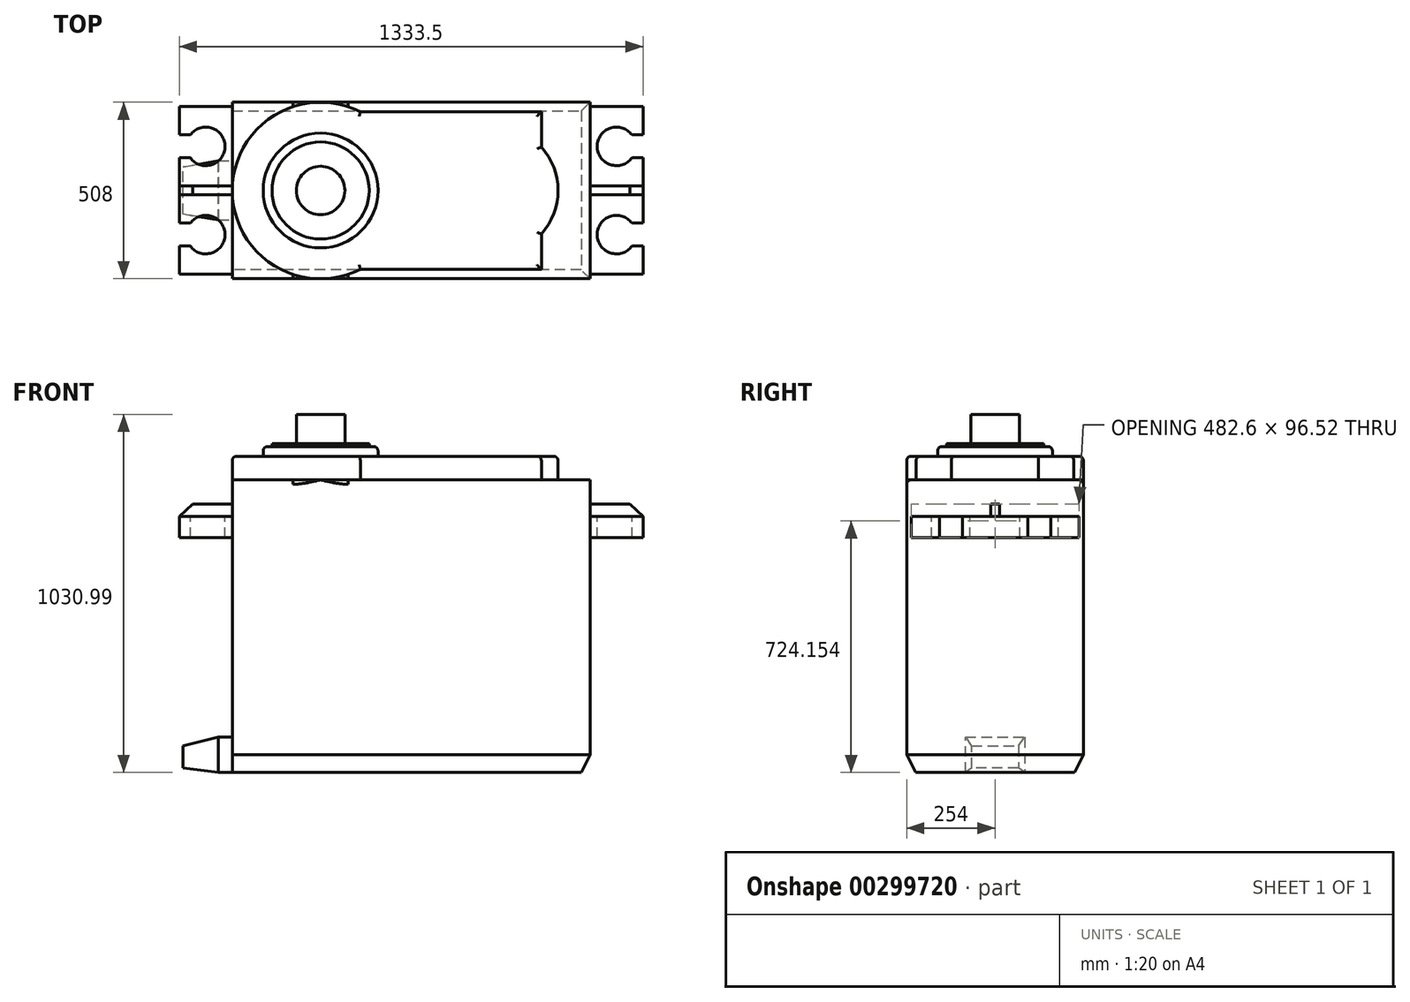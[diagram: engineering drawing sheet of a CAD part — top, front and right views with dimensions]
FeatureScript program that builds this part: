
annotation { "Feature Type Name" : "Feature", "Feature Type Description" : "" }
export const myFeature = defineFeature(function(context is Context, id is Id, definition is map)
    precondition{}
    {
        {
            var Q0;
            Q0=qCreatedBy(makeId("Front.planeOp"),FACE);
            var sketch = newSketch(context, id + "F0", { "sketchPlane" : qUnion([Q0])});
            skLineSegment(sketch, "E0", {"start": v(0, 0) * mm, "end": v(514.35, 0) * mm});
            skLineSegment(sketch, "E1.MirrorCS", {"start": v(0, 0) * mm, "end": v(-514.35, 0) * mm});
            skLineSegment(sketch, "E2", {"start": v(514.35, 0) * mm, "end": v(514.35, 842.26) * mm});
            skLineSegment(sketch, "E3", {"start": v(514.35, 842.26) * mm, "end": v(-514.35, 842.26) * mm});
            skLineSegment(sketch, "E4", {"start": v(-514.35, 842.26) * mm, "end": v(-514.35, 0) * mm});
            skSolve(sketch);
        }
        {
            var Q0;
            Q0 = qSketchRegion(id + "F0", true);
            extrude(context, id + "F1", {"entities" : qUnion([Q0]), "endBound" : BoundingType.SYMMETRIC, "depth" : 508 * mm});
        }
        {
            var Q0;
            Q0=makeQuery(id+"F1.opExtrude","CAP_EDGE",EDGE,{"disambiguationData":[OSD([sQuery(id+"F0.wireOp",EDGE,"E0"),sQuery(id+"F0.wireOp",EDGE,"E1.MirrorCS")])],"isStart":false});
            var Q1;
            Q1=makeQuery(id+"F1.opExtrude","SWEPT_EDGE",EDGE,{"disambiguationData":[OSD([sQuery(id+"F0.wireOp",EDGE,"E0"),sQuery(id+"F0.wireOp",EDGE,"E2")])]});
            var Q2;
            Q2=makeQuery(id+"F1.opExtrude","CAP_EDGE",EDGE,{"disambiguationData":[OSD([sQuery(id+"F0.wireOp",EDGE,"E0"),sQuery(id+"F0.wireOp",EDGE,"E1.MirrorCS")])],"isStart":true});
            chamfer(context, id + "F2", {"entities" : qUnion([Q0, Q1, Q2]), "chamferType" : ChamferType.OFFSET_ANGLE, "width" : 25.4 * mm, "oppositeDirection" : false, "angle" : 63.4 * degree, "tangentPropagation" : true});
        }
        {
            var Q0;
            Q0=makeQuery(id+"F1.opExtrude","SWEPT_FACE",FACE,{"disambiguationData":[OSD([sQuery(id+"F0.wireOp",EDGE,"E4")])]});
            var sketch = newSketch(context, id + "F3", { "sketchPlane" : qUnion([Q0])});
            skLineSegment(sketch, "E5", {"start": v(-85.09, 0) * mm, "end": v(85.1, 0) * mm});
            skLineSegment(sketch, "E6", {"start": v(85.1, 0) * mm, "end": v(85.1, 101.6) * mm});
            skLineSegment(sketch, "E7", {"start": v(85.1, 101.6) * mm, "end": v(-85.09, 101.6) * mm});
            skLineSegment(sketch, "E8", {"start": v(-85.09, 101.6) * mm, "end": v(-85.09, 0) * mm});
            skSolve(sketch);
        }
        {
            var Q0;
            Q0 = qSketchRegion(id + "F3", true);
            extrude(context, id + "F4", {"entities" : qUnion([Q0]), "operationType" : NewBodyOperationType.ADD, "depth" : 142.24 * mm});
        }
        {
            var Q0;
            Q0=makeQuery(id+"F4.opExtrude","CAP_EDGE",EDGE,{"disambiguationData":[OSD([sQuery(id+"F3.wireOp",EDGE,"E5")])],"isStart":false});
            chamfer(context, id + "F5", {"entities" : qUnion([Q0]), "chamferType" : ChamferType.TWO_OFFSETS, "width1" : 101.6 * mm, "oppositeDirection" : false, "width2" : 12.7 * mm, "tangentPropagation" : true});
        }
        {
            var Q0;
            Q0=makeQuery(id+"F4.opExtrude","CAP_EDGE",EDGE,{"disambiguationData":[OSD([sQuery(id+"F3.wireOp",EDGE,"E6")])],"isStart":false});
            var Q1;
            Q1=makeQuery(id+"F4.opExtrude","CAP_EDGE",EDGE,{"disambiguationData":[OSD([sQuery(id+"F3.wireOp",EDGE,"E8")])],"isStart":false});
            chamfer(context, id + "F6", {"entities" : qUnion([Q0, Q1]), "chamferType" : ChamferType.TWO_OFFSETS, "width1" : 101.6 * mm, "oppositeDirection" : true, "width2" : 17.78 * mm, "tangentPropagation" : true});
        }
        {
            var Q0;
            Q0=makeQuery(id+"F4.opExtrude","CAP_EDGE",EDGE,{"disambiguationData":[OSD([sQuery(id+"F3.wireOp",EDGE,"E7")])],"isStart":false});
            chamfer(context, id + "F7", {"entities" : qUnion([Q0]), "chamferType" : ChamferType.TWO_OFFSETS, "width1" : 101.6 * mm, "oppositeDirection" : true, "width2" : 25.4 * mm, "tangentPropagation" : true});
        }
        {
            var Q0;
            Q0=makeQuery(id+"F1.opExtrude","SWEPT_FACE",FACE,{"disambiguationData":[OSD([sQuery(id+"F0.wireOp",EDGE,"E3")])]});
            var sketch = newSketch(context, id + "F8", { "sketchPlane" : qUnion([Q0])});
            skLineSegment(sketch, "E9", {"start": v(514.35, 0) * mm, "end": v(514.35, -241.3) * mm});
            skLineSegment(sketch, "E10", {"start": v(514.35, -241.3) * mm, "end": v(666.75, -241.3) * mm});
            skLineSegment(sketch, "E11", {"start": v(666.75, -241.3) * mm, "end": v(666.75, -160.02) * mm});
            skArc(sketch, "E12", {"start": v(635, -160.02) * mm, "mid": v(535.18, -127) * mm, "end": v(635, -93.98) * mm});
            skLineSegment(sketch, "E13", {"start": v(635, -160.02) * mm, "end": v(666.75, -160.02) * mm});
            skLineSegment(sketch, "E14", {"start": v(666.75, -93.98) * mm, "end": v(666.75, 0) * mm});
            skLineSegment(sketch, "E15", {"start": v(666.75, -93.98) * mm, "end": v(635, -93.98) * mm});
            skLineSegment(sketch, "E16", {"start": v(514.35, 0) * mm, "end": v(563.65, 0) * mm});
            skLineSegment(sketch, "E17.MirrorCS", {"start": v(514.35, 0) * mm, "end": v(514.35, 241.3) * mm});
            skLineSegment(sketch, "E18.MirrorCS", {"start": v(514.35, 241.3) * mm, "end": v(666.75, 241.3) * mm});
            skLineSegment(sketch, "E19.MirrorCS", {"start": v(666.75, 241.3) * mm, "end": v(666.75, 160.02) * mm});
            skArc(sketch, "E20.MirrorCS", {"start": v(635, 160.02) * mm, "mid": v(535.18, 127) * mm, "end": v(635, 93.98) * mm});
            skLineSegment(sketch, "E21.MirrorCS", {"start": v(666.75, 93.98) * mm, "end": v(666.75, 0) * mm});
            skLineSegment(sketch, "E22.MirrorCS", {"start": v(666.75, 93.98) * mm, "end": v(635, 93.98) * mm});
            skLineSegment(sketch, "E23.MirrorCS", {"start": v(635, 160.02) * mm, "end": v(666.75, 160.02) * mm});
            skLineSegment(sketch, "E24", {"start": v(0, 0) * mm, "end": v(0, -87.43) * mm});
            skLineSegment(sketch, "E25.MirrorCS", {"start": v(-514.35, 0) * mm, "end": v(-514.35, 241.3) * mm});
            skLineSegment(sketch, "E26.MirrorCS", {"start": v(-514.35, 0) * mm, "end": v(-514.35, -241.3) * mm});
            skLineSegment(sketch, "E27.MirrorCS", {"start": v(-666.75, -93.98) * mm, "end": v(-635, -93.98) * mm});
            skLineSegment(sketch, "E28.MirrorCS", {"start": v(-635, -160.02) * mm, "end": v(-666.75, -160.02) * mm});
            skLineSegment(sketch, "E29.MirrorCS", {"start": v(-635, 160.02) * mm, "end": v(-666.75, 160.02) * mm});
            skLineSegment(sketch, "E30.MirrorCS", {"start": v(-666.75, 93.98) * mm, "end": v(-635, 93.98) * mm});
            skLineSegment(sketch, "E31.MirrorCS", {"start": v(-514.35, 0) * mm, "end": v(-563.65, 0) * mm});
            skLineSegment(sketch, "E32.MirrorCS", {"start": v(-514.35, 241.3) * mm, "end": v(-666.75, 241.3) * mm});
            skLineSegment(sketch, "E33.MirrorCS", {"start": v(-666.75, 241.3) * mm, "end": v(-666.75, 160.02) * mm});
            skArc(sketch, "E34.MirrorCS", {"start": v(-635, 160.02) * mm, "mid": v(-535.18, 127) * mm, "end": v(-635, 93.98) * mm});
            skLineSegment(sketch, "E35.MirrorCS", {"start": v(-666.75, -93.98) * mm, "end": v(-666.75, 0) * mm});
            skLineSegment(sketch, "E36.MirrorCS", {"start": v(-666.75, 93.98) * mm, "end": v(-666.75, 0) * mm});
            skArc(sketch, "E37.MirrorCS", {"start": v(-635, -160.02) * mm, "mid": v(-535.18, -127) * mm, "end": v(-635, -93.98) * mm});
            skLineSegment(sketch, "E38.MirrorCS", {"start": v(-666.75, -241.3) * mm, "end": v(-666.75, -160.02) * mm});
            skLineSegment(sketch, "E39.MirrorCS", {"start": v(-514.35, -241.3) * mm, "end": v(-666.75, -241.3) * mm});
            skSolve(sketch);
        }
        {
            var Q0;
            Q0 = qSketchRegion(id + "F8", true);
            extrude(context, id + "F9", {"entities" : qUnion([Q0]), "operationType" : NewBodyOperationType.ADD, "oppositeDirection" : true, "depth" : 166.37 * mm});
        }
        {
            var Q0;
            Q0=makeQuery(id+"F8.imprint","IMPRINT",FACE,{"disambiguationData":[TD([[makeQuery(id+"F8.imprint","IMPRINT",EDGE,{"derivedFrom":sQuery(id+"F8.wireOp",EDGE,"E27.MirrorCS")}),1.0]])]});
            var Q1;
            Q1=makeQuery(id+"F8.imprint","IMPRINT",FACE,{"disambiguationData":[TD([[makeQuery(id+"F8.imprint","IMPRINT",EDGE,{"derivedFrom":sQuery(id+"F8.wireOp",EDGE,"E9")}),-1.0]])]});
            extrude(context, id + "F10", {"entities" : qUnion([Q0, Q1]), "operationType" : NewBodyOperationType.REMOVE, "oppositeDirection" : true, "depth" : 105.4 * mm});
        }
        {
            var Q0;
            Q0=makeQuery(id+"F10.boolean.opBoolean","COPY",FACE,{"derivedFrom":makeQuery(id+"F10.opExtrude","CAP_FACE",FACE,{"disambiguationData":[OSD([sQuery(id+"F8.wireOp",EDGE,"E9"),sQuery(id+"F8.wireOp",EDGE,"E10"),sQuery(id+"F8.wireOp",EDGE,"E11"),sQuery(id+"F8.wireOp",EDGE,"E12"),sQuery(id+"F8.wireOp",EDGE,"E13"),sQuery(id+"F8.wireOp",EDGE,"E14"),sQuery(id+"F8.wireOp",EDGE,"E15"),sQuery(id+"F8.wireOp",EDGE,"E17.MirrorCS"),sQuery(id+"F8.wireOp",EDGE,"E18.MirrorCS"),sQuery(id+"F8.wireOp",EDGE,"E19.MirrorCS"),sQuery(id+"F8.wireOp",EDGE,"E20.MirrorCS"),sQuery(id+"F8.wireOp",EDGE,"E21.MirrorCS"),sQuery(id+"F8.wireOp",EDGE,"E22.MirrorCS"),sQuery(id+"F8.wireOp",EDGE,"E23.MirrorCS")])],"isStart":false})});
            var sketch = newSketch(context, id + "F11", { "sketchPlane" : qUnion([Q0])});
            skLineSegment(sketch, "E40", {"start": v(514.35, -12.7) * mm, "end": v(666.75, -12.7) * mm});
            skLineSegment(sketch, "E41", {"start": v(666.75, -12.7) * mm, "end": v(666.75, 12.7) * mm});
            skLineSegment(sketch, "E42", {"start": v(666.75, 12.7) * mm, "end": v(514.35, 12.7) * mm});
            skLineSegment(sketch, "E43", {"start": v(514.35, 12.7) * mm, "end": v(514.35, -12.7) * mm});
            skLineSegment(sketch, "E44", {"start": v(0, 0) * mm, "end": v(0, 98.08) * mm});
            skLineSegment(sketch, "E45.MirrorCS", {"start": v(-666.75, -12.7) * mm, "end": v(-666.75, 12.7) * mm});
            skLineSegment(sketch, "E46.MirrorCS", {"start": v(-514.35, 12.7) * mm, "end": v(-514.35, -12.7) * mm});
            skLineSegment(sketch, "E47.MirrorCS", {"start": v(-514.35, -12.7) * mm, "end": v(-666.75, -12.7) * mm});
            skLineSegment(sketch, "E48.MirrorCS", {"start": v(-666.75, 12.7) * mm, "end": v(-514.35, 12.7) * mm});
            skSolve(sketch);
        }
        {
            var Q0;
            Q0 = qSketchRegion(id + "F11", true);
            extrude(context, id + "F12", {"entities" : qUnion([Q0]), "operationType" : NewBodyOperationType.ADD, "depth" : 35.56 * mm});
        }
        {
            var Q0;
            Q0=makeQuery(id+"F12.opExtrude","CAP_EDGE",EDGE,{"disambiguationData":[OSD([sQuery(id+"F11.wireOp",EDGE,"E41")])],"isStart":false});
            chamfer(context, id + "F13", {"entities" : qUnion([Q0]), "chamferType" : ChamferType.TWO_OFFSETS, "width1" : 35.56 * mm, "oppositeDirection" : true, "width2" : 38.1 * mm, "tangentPropagation" : true});
        }
        {
            var Q0;
            Q0=makeQuery(id+"F12.opExtrude","CAP_EDGE",EDGE,{"disambiguationData":[OSD([sQuery(id+"F11.wireOp",EDGE,"E45.MirrorCS")])],"isStart":false});
            chamfer(context, id + "F14", {"entities" : qUnion([Q0]), "chamferType" : ChamferType.TWO_OFFSETS, "width1" : 35.56 * mm, "oppositeDirection" : false, "width2" : 38.1 * mm, "tangentPropagation" : true});
        }
        {
            var Q0;
            Q0=makeQuery(id+"F9.boolean.opBoolean","MERGE",FACE,{"derivedFrom":[makeQuery(id+"F1.opExtrude","SWEPT_FACE",FACE,{"disambiguationData":[OSD([sQuery(id+"F0.wireOp",EDGE,"E3")])]}),makeQuery(id+"F9.opExtrude","CAP_FACE",FACE,{"disambiguationData":[OSD([sQuery(id+"F8.wireOp",EDGE,"E9"),sQuery(id+"F8.wireOp",EDGE,"E10"),sQuery(id+"F8.wireOp",EDGE,"E11"),sQuery(id+"F8.wireOp",EDGE,"E12"),sQuery(id+"F8.wireOp",EDGE,"E13"),sQuery(id+"F8.wireOp",EDGE,"E14"),sQuery(id+"F8.wireOp",EDGE,"E15"),sQuery(id+"F8.wireOp",EDGE,"E17.MirrorCS"),sQuery(id+"F8.wireOp",EDGE,"E18.MirrorCS"),sQuery(id+"F8.wireOp",EDGE,"E19.MirrorCS"),sQuery(id+"F8.wireOp",EDGE,"E20.MirrorCS"),sQuery(id+"F8.wireOp",EDGE,"E21.MirrorCS"),sQuery(id+"F8.wireOp",EDGE,"E22.MirrorCS"),sQuery(id+"F8.wireOp",EDGE,"E23.MirrorCS")])],"isStart":true}),makeQuery(id+"F9.opExtrude","CAP_FACE",FACE,{"disambiguationData":[OSD([sQuery(id+"F8.wireOp",EDGE,"E27.MirrorCS"),sQuery(id+"F8.wireOp",EDGE,"E28.MirrorCS"),sQuery(id+"F8.wireOp",EDGE,"E29.MirrorCS"),sQuery(id+"F8.wireOp",EDGE,"E30.MirrorCS"),sQuery(id+"F8.wireOp",EDGE,"E25.MirrorCS"),sQuery(id+"F8.wireOp",EDGE,"E32.MirrorCS"),sQuery(id+"F8.wireOp",EDGE,"E33.MirrorCS"),sQuery(id+"F8.wireOp",EDGE,"E34.MirrorCS"),sQuery(id+"F8.wireOp",EDGE,"E35.MirrorCS"),sQuery(id+"F8.wireOp",EDGE,"E36.MirrorCS"),sQuery(id+"F8.wireOp",EDGE,"E37.MirrorCS"),sQuery(id+"F8.wireOp",EDGE,"E38.MirrorCS"),sQuery(id+"F8.wireOp",EDGE,"E39.MirrorCS"),sQuery(id+"F8.wireOp",EDGE,"E26.MirrorCS")])],"isStart":true})]});
            var sketch = newSketch(context, id + "F15", { "sketchPlane" : qUnion([Q0])});
            skPoint(sketch, "E49", {"position": v(374.65, -226.82) * mm});
            skArc(sketch, "E50", {"start": v(-514.35, 0) * mm, "mid": v(-393.54, -216.28) * mm, "end": v(-146.04, -226.82) * mm});
            skLineSegment(sketch, "E51", {"start": v(-146.04, -226.82) * mm, "end": v(374.65, -226.82) * mm});
            skLineSegment(sketch, "E52", {"start": v(374.65, -226.82) * mm, "end": v(374.65, -125.18) * mm});
            skArc(sketch, "E53", {"start": v(374.65, -125.18) * mm, "mid": v(410.06, -67) * mm, "end": v(422.4, 0) * mm});
            skLineSegment(sketch, "E54", {"start": v(0, 0) * mm, "end": v(-165.98, 0) * mm});
            skPoint(sketch, "E55.MirrorP", {"position": v(374.65, 226.82) * mm});
            skArc(sketch, "E56.MirrorCS", {"start": v(-514.35, 0) * mm, "mid": v(-393.54, 216.28) * mm, "end": v(-146.04, 226.82) * mm});
            skLineSegment(sketch, "E57.MirrorCS", {"start": v(-146.04, 226.82) * mm, "end": v(374.65, 226.82) * mm});
            skLineSegment(sketch, "E58.MirrorCS", {"start": v(374.65, 226.82) * mm, "end": v(374.65, 125.18) * mm});
            skArc(sketch, "E59.MirrorCS", {"start": v(374.65, 125.18) * mm, "mid": v(410.06, 67) * mm, "end": v(422.4, 0) * mm});
            skCircle(sketch, "E60", {"center": v(-260.35, 0) * mm, "radius": 165.1 * mm});
            skCircle(sketch, "E61", {"center": v(-260.35, 0) * mm, "radius": 139.7 * mm});
            skCircle(sketch, "E62", {"center": v(-260.35, 0) * mm, "radius": 69.85 * mm});
            skSolve(sketch);
        }
        {
            var Q0;
            Q0 = qSketchRegion(id + "F15", true);
            extrude(context, id + "F16", {"entities" : qUnion([Q0]), "operationType" : NewBodyOperationType.ADD, "depth" : 68.07 * mm});
        }
        {
            var Q0;
            Q0=makeQuery(id+"F15.imprint","IMPRINT",FACE,{"disambiguationData":[TD([[makeQuery(id+"F15.imprint","IMPRINT",EDGE,{"derivedFrom":sQuery(id+"F15.wireOp",EDGE,"E60")}),1.0]])]});
            extrude(context, id + "F17", {"entities" : qUnion([Q0]), "operationType" : NewBodyOperationType.ADD, "depth" : 96.01 * mm});
        }
        {
            var Q0;
            Q0=makeQuery(id+"F15.imprint","IMPRINT",FACE,{"disambiguationData":[TD([[makeQuery(id+"F15.imprint","IMPRINT",EDGE,{"derivedFrom":sQuery(id+"F15.wireOp",EDGE,"E61")}),1.0]])]});
            extrude(context, id + "F18", {"entities" : qUnion([Q0]), "operationType" : NewBodyOperationType.ADD, "depth" : 104.9 * mm});
        }
        {
            var Q0;
            Q0=makeQuery(id+"F15.imprint","IMPRINT",FACE,{"disambiguationData":[TD([[makeQuery(id+"F15.imprint","IMPRINT",EDGE,{"derivedFrom":sQuery(id+"F15.wireOp",EDGE,"E62")}),1.0]])]});
            extrude(context, id + "F19", {"entities" : qUnion([Q0]), "operationType" : NewBodyOperationType.ADD, "depth" : 188.72 * mm});
        }
        {
            var Q0;
            {var subQ0=sQuery(id+"F0.wireOp",EDGE,"E4");var subQ1=sQuery(id+"F0.wireOp",EDGE,"E3");Q0=makeQuery(id+"F16.boolean.opBoolean","SPLIT",EDGE,{"disambiguationData":[TD([makeQuery(id+"F1.opExtrude","SWEPT_FACE",FACE,{"disambiguationData":[OSD([subQ0])]})])],"derivedFrom":makeQuery(id+"F1.opExtrude","CAP_EDGE",EDGE,{"disambiguationData":[OSD([subQ1])],"isStart":false})});}
            var Q1;
            {var subQ2=sQuery(id+"F0.wireOp",EDGE,"E3");var subQ3=sQuery(id+"F0.wireOp",EDGE,"E2");Q1=makeQuery(id+"F16.boolean.opBoolean","SPLIT",EDGE,{"disambiguationData":[TD([makeQuery(id+"F1.opExtrude","SWEPT_FACE",FACE,{"disambiguationData":[OSD([subQ3])]})])],"derivedFrom":makeQuery(id+"F1.opExtrude","CAP_EDGE",EDGE,{"disambiguationData":[OSD([subQ2])],"isStart":false})});}
            var Q2;
            {var subQ0=sQuery(id+"F8.wireOp",EDGE,"E17.MirrorCS");var subQ1=sQuery(id+"F8.wireOp",EDGE,"E9");var subQ2=sQuery(id+"F8.wireOp",EDGE,"E18.MirrorCS");var subQ3=sQuery(id+"F8.wireOp",EDGE,"E10");var subQ5=sQuery(id+"F0.wireOp",EDGE,"E3");var subQ8=sQuery(id+"F0.wireOp",EDGE,"E2");var subQ13=makeQuery(id+"F1.opExtrude","SWEPT_EDGE",EDGE,{"disambiguationData":[OSD([subQ8,subQ5])]});Q2=makeQuery(id+"F10.boolean.opBoolean","MERGE",EDGE,{"derivedFrom":[makeQuery(id+"F9.boolean.opBoolean","SPLIT",EDGE,{"disambiguationData":[TD([makeQuery(id+"F9.opExtrude","SWEPT_FACE",FACE,{"disambiguationData":[OSD([subQ2])]})])],"derivedFrom":subQ13}),makeQuery(id+"F9.boolean.opBoolean","SPLIT",EDGE,{"disambiguationData":[TD([makeQuery(id+"F9.opExtrude","SWEPT_FACE",FACE,{"disambiguationData":[OSD([subQ3])]})])],"derivedFrom":subQ13}),makeQuery(id+"F10.opExtrude","CAP_EDGE",EDGE,{"disambiguationData":[OSD([subQ1,subQ0])],"isStart":true})]});}
            var Q3;
            {var subQ0=sQuery(id+"F0.wireOp",EDGE,"E3");var subQ1=sQuery(id+"F0.wireOp",EDGE,"E2");Q3=makeQuery(id+"F16.boolean.opBoolean","SPLIT",EDGE,{"disambiguationData":[TD([makeQuery(id+"F1.opExtrude","SWEPT_FACE",FACE,{"disambiguationData":[OSD([subQ1])]})])],"derivedFrom":makeQuery(id+"F1.opExtrude","CAP_EDGE",EDGE,{"disambiguationData":[OSD([subQ0])],"isStart":true})});}
            var Q4;
            {var subQ0=sQuery(id+"F0.wireOp",EDGE,"E4");var subQ1=sQuery(id+"F0.wireOp",EDGE,"E3");Q4=makeQuery(id+"F16.boolean.opBoolean","SPLIT",EDGE,{"disambiguationData":[TD([makeQuery(id+"F1.opExtrude","SWEPT_FACE",FACE,{"disambiguationData":[OSD([subQ0])]})])],"derivedFrom":makeQuery(id+"F1.opExtrude","CAP_EDGE",EDGE,{"disambiguationData":[OSD([subQ1])],"isStart":true})});}
            var Q5;
            {var subQ1=sQuery(id+"F0.wireOp",EDGE,"E4");var subQ3=sQuery(id+"F0.wireOp",EDGE,"E3");var subQ5=sQuery(id+"F8.wireOp",EDGE,"E26.MirrorCS");var subQ6=sQuery(id+"F8.wireOp",EDGE,"E39.MirrorCS");var subQ7=sQuery(id+"F8.wireOp",EDGE,"E32.MirrorCS");var subQ8=sQuery(id+"F8.wireOp",EDGE,"E25.MirrorCS");var subQ10=sQuery(id+"F0.wireOp",EDGE,"E2");var subQ11=sQuery(id+"F0.wireOp",EDGE,"E1.MirrorCS");var subQ12=sQuery(id+"F0.wireOp",EDGE,"E0");var subQ13=makeQuery(id+"F1.opExtrude","CAP_FACE",FACE,{"disambiguationData":[OSD([subQ12,subQ11,subQ10,subQ3,subQ1])],"isStart":false});var subQ14=makeQuery(id+"F1.opExtrude","SWEPT_EDGE",EDGE,{"disambiguationData":[OSD([subQ3,subQ1])]});Q5=makeQuery(id+"F16.boolean.opBoolean","SPLIT",EDGE,{"disambiguationData":[TD([subQ13])],"derivedFrom":makeQuery(id+"F10.boolean.opBoolean","MERGE",EDGE,{"derivedFrom":[makeQuery(id+"F9.boolean.opBoolean","SPLIT",EDGE,{"disambiguationData":[TD([makeQuery(id+"F9.opExtrude","SWEPT_FACE",FACE,{"disambiguationData":[OSD([subQ7])]})])],"derivedFrom":subQ14}),makeQuery(id+"F9.boolean.opBoolean","SPLIT",EDGE,{"disambiguationData":[TD([makeQuery(id+"F9.opExtrude","SWEPT_FACE",FACE,{"disambiguationData":[OSD([subQ6])]})])],"derivedFrom":subQ14}),makeQuery(id+"F10.opExtrude","CAP_EDGE",EDGE,{"disambiguationData":[OSD([subQ8,subQ5])],"isStart":true})]})});}
            var Q6;
            {var subQ0=sQuery(id+"F0.wireOp",EDGE,"E4");var subQ2=sQuery(id+"F0.wireOp",EDGE,"E3");var subQ4=sQuery(id+"F8.wireOp",EDGE,"E26.MirrorCS");var subQ5=sQuery(id+"F8.wireOp",EDGE,"E39.MirrorCS");var subQ6=sQuery(id+"F8.wireOp",EDGE,"E32.MirrorCS");var subQ7=sQuery(id+"F8.wireOp",EDGE,"E25.MirrorCS");var subQ10=sQuery(id+"F0.wireOp",EDGE,"E2");var subQ11=sQuery(id+"F0.wireOp",EDGE,"E1.MirrorCS");var subQ12=sQuery(id+"F0.wireOp",EDGE,"E0");var subQ13=makeQuery(id+"F1.opExtrude","CAP_FACE",FACE,{"disambiguationData":[OSD([subQ12,subQ11,subQ10,subQ2,subQ0])],"isStart":true});var subQ14=makeQuery(id+"F1.opExtrude","SWEPT_EDGE",EDGE,{"disambiguationData":[OSD([subQ2,subQ0])]});Q6=makeQuery(id+"F16.boolean.opBoolean","SPLIT",EDGE,{"disambiguationData":[TD([subQ13])],"derivedFrom":makeQuery(id+"F10.boolean.opBoolean","MERGE",EDGE,{"derivedFrom":[makeQuery(id+"F9.boolean.opBoolean","SPLIT",EDGE,{"disambiguationData":[TD([makeQuery(id+"F9.opExtrude","SWEPT_FACE",FACE,{"disambiguationData":[OSD([subQ6])]})])],"derivedFrom":subQ14}),makeQuery(id+"F9.boolean.opBoolean","SPLIT",EDGE,{"disambiguationData":[TD([makeQuery(id+"F9.opExtrude","SWEPT_FACE",FACE,{"disambiguationData":[OSD([subQ5])]})])],"derivedFrom":subQ14}),makeQuery(id+"F10.opExtrude","CAP_EDGE",EDGE,{"disambiguationData":[OSD([subQ7,subQ4])],"isStart":true})]})});}
            var Q7;
            Q7=makeQuery(id+"F16.opExtrude","CAP_EDGE",EDGE,{"disambiguationData":[OSD([sQuery(id+"F15.wireOp",EDGE,"E50"),sQuery(id+"F15.wireOp",EDGE,"E56.MirrorCS")])],"isStart":false});
            var Q8;
            Q8=makeQuery(id+"F16.opExtrude","CAP_EDGE",EDGE,{"disambiguationData":[OSD([sQuery(id+"F15.wireOp",EDGE,"E57.MirrorCS")])],"isStart":false});
            var Q9;
            Q9=makeQuery(id+"F16.opExtrude","CAP_EDGE",EDGE,{"disambiguationData":[OSD([sQuery(id+"F15.wireOp",EDGE,"E51")])],"isStart":false});
            var Q10;
            Q10=makeQuery(id+"F16.opExtrude","CAP_EDGE",EDGE,{"disambiguationData":[OSD([sQuery(id+"F15.wireOp",EDGE,"E52")])],"isStart":false});
            var Q11;
            Q11=makeQuery(id+"F16.opExtrude","CAP_EDGE",EDGE,{"disambiguationData":[OSD([sQuery(id+"F15.wireOp",EDGE,"E53"),sQuery(id+"F15.wireOp",EDGE,"E59.MirrorCS")])],"isStart":false});
            var Q12;
            Q12=makeQuery(id+"F16.opExtrude","CAP_EDGE",EDGE,{"disambiguationData":[OSD([sQuery(id+"F15.wireOp",EDGE,"E58.MirrorCS")])],"isStart":false});
            var Q13;
            Q13=makeQuery(id+"F17.opExtrude","CAP_EDGE",EDGE,{"disambiguationData":[OSD([sQuery(id+"F15.wireOp",EDGE,"E60")])],"isStart":false});
            fillet(context, id + "F20", {"entities" : qUnion([Q0, Q1, Q2, Q3, Q4, Q5, Q6, Q7, Q8, Q9, Q10, Q11, Q12, Q13]), "radius" : 12.7 * mm, "tangentPropagation" : true, "allowEdgeOverflow" : false});
        }
    });
